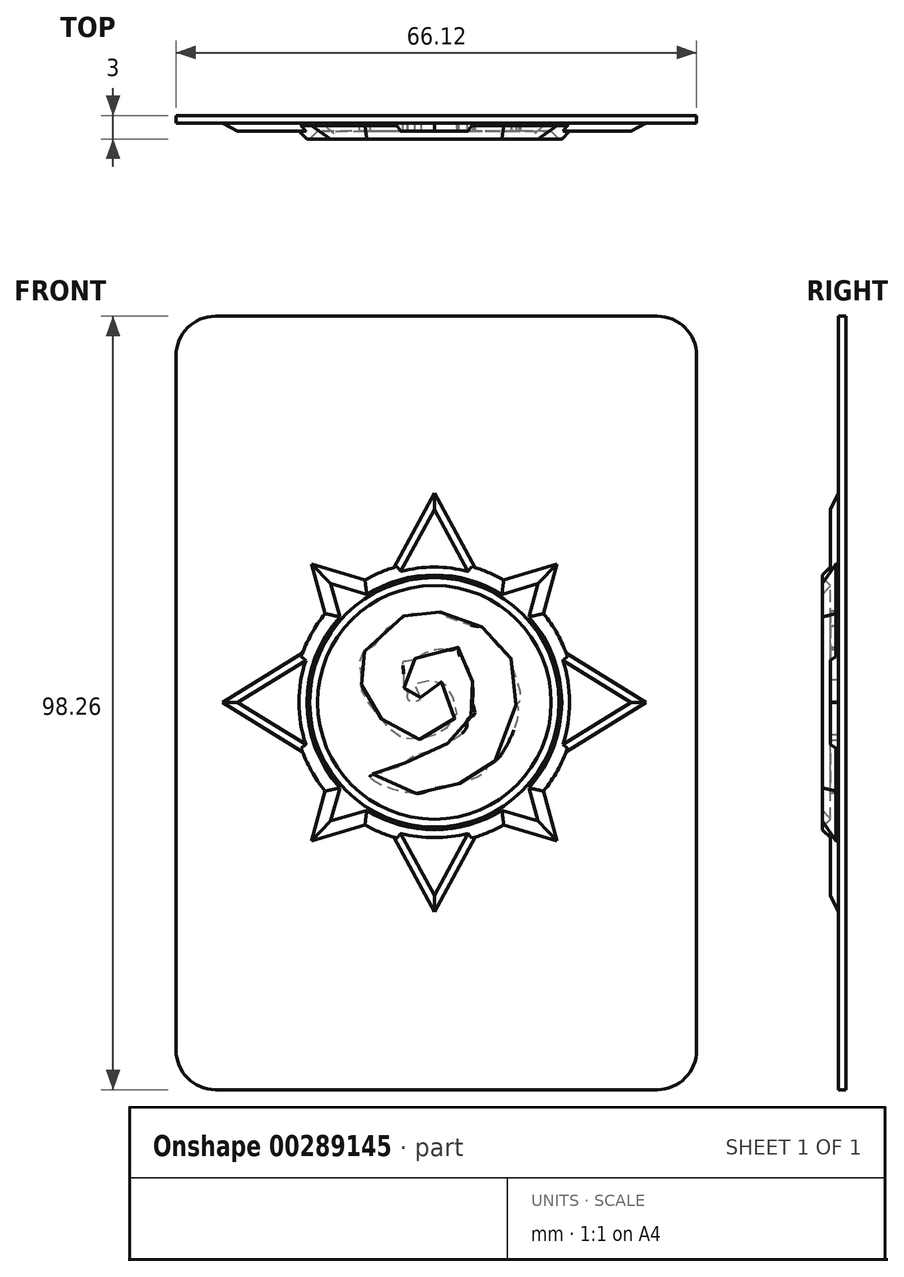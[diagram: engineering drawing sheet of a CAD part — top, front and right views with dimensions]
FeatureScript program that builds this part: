
annotation { "Feature Type Name" : "Feature", "Feature Type Description" : "" }
export const myFeature = defineFeature(function(context is Context, id is Id, definition is map)
    precondition{}
    {
        {
            var Q0;
            Q0=qCreatedBy(makeId("Front.planeOp"),FACE);
            var sketch = newSketch(context, id + "F0", { "sketchPlane" : qUnion([Q0])});
            skArc(sketch, "E0", {"start": v(14.14, 0) * mm, "mid": v(10, 10) * mm, "end": v(0, 14.14) * mm});
            skArc(sketch, "E1", {"start": v(17.88, 0) * mm, "mid": v(12.64, 12.64) * mm, "end": v(0, 17.88) * mm});
            skArc(sketch, "E2", {"start": v(15.77, 0) * mm, "mid": v(11.15, 11.15) * mm, "end": v(0, 15.77) * mm});
            skLineSegment(sketch, "E3", {"start": v(10.28, 11.96) * mm, "end": v(15.6, 17.6) * mm});
            skLineSegment(sketch, "E4", {"start": v(15.6, 17.6) * mm, "end": v(8.8, 15.56) * mm});
            skLineSegment(sketch, "E5", {"start": v(15.6, 17.6) * mm, "end": v(13.88, 11.27) * mm});
            skLineSegment(sketch, "E6", {"start": v(5.15, 17.13) * mm, "end": v(0, 26.62) * mm});
            skLineSegment(sketch, "E7", {"start": v(16.75, 6.27) * mm, "end": v(26.88, 0) * mm});
            skLineSegment(sketch, "E8", {"start": v(0, 26.62) * mm, "end": v(0, 0) * mm});
            skLineSegment(sketch, "E9", {"start": v(26.88, 0) * mm, "end": v(0, 0) * mm});
            skSolve(sketch);
        }
        {
            var Q0;
            {var subQ0=sQuery(id+"F0.wireOp",EDGE,"E0");Q0=makeQuery(id+"F0.imprint","IMPRINT",FACE,{"disambiguationData":[TD([[makeQuery(id+"F0.imprint","IMPRINT",EDGE,{"derivedFrom":subQ0}),1.0]])]});}
            extrude(context, id + "F1", {"entities" : qUnion([Q0]), "depth" : 1 * mm});
        }
        {
            var Q0;
            {var subQ4=sQuery(id+"F0.wireOp",EDGE,"E0");Q0=makeQuery(id+"F0.imprint","IMPRINT",FACE,{"disambiguationData":[TD([[makeQuery(id+"F0.imprint","IMPRINT",EDGE,{"derivedFrom":subQ4}),-1.0]])]});}
            extrude(context, id + "F2", {"entities" : qUnion([Q0]), "operationType" : NewBodyOperationType.ADD, "depth" : 2 * mm});
        }
        {
            var Q0;
            {var subQ0=sQuery(id+"F0.wireOp",EDGE,"E1");var subQ4=sQuery(id+"F0.wireOp",EDGE,"E9");var subQ9=makeQuery(id+"F0.imprint","INTERSECT",VERTEX,{"derivedFrom":[subQ0,subQ4]});Q0=makeQuery(id+"F0.imprint","IMPRINT",FACE,{"disambiguationData":[TD([[makeQuery(id+"F0.imprint","IMPRINT",EDGE,{"disambiguationData":[TD([[subQ9,-1.0]])],"derivedFrom":subQ0}),1.0]])]});}
            var Q1;
            {var subQ5=sQuery(id+"F0.wireOp",EDGE,"E1");var subQ8=makeQuery(id+"F0.imprint","INTERSECT",VERTEX,{"derivedFrom":[subQ5,sQuery(id+"F0.wireOp",EDGE,"E4")]});Q1=makeQuery(id+"F0.imprint","IMPRINT",FACE,{"disambiguationData":[TD([[makeQuery(id+"F0.imprint","IMPRINT",EDGE,{"disambiguationData":[TD([[subQ8,1.0]])],"derivedFrom":subQ5}),1.0]])]});}
            extrude(context, id + "F3", {"entities" : qUnion([Q0, Q1]), "operationType" : NewBodyOperationType.ADD, "depth" : 2 * mm});
        }
        {
            var Q0;
            {var subQ3=sQuery(id+"F0.wireOp",EDGE,"E7");Q0=makeQuery(id+"F0.imprint","IMPRINT",FACE,{"disambiguationData":[TD([[makeQuery(id+"F0.imprint","IMPRINT",EDGE,{"derivedFrom":subQ3}),-1.0]])]});}
            var Q1;
            {var subQ3=sQuery(id+"F0.wireOp",EDGE,"E6");Q1=makeQuery(id+"F0.imprint","IMPRINT",FACE,{"disambiguationData":[TD([[makeQuery(id+"F0.imprint","IMPRINT",EDGE,{"derivedFrom":subQ3}),1.0]])]});}
            extrude(context, id + "F4", {"entities" : qUnion([Q0, Q1]), "operationType" : NewBodyOperationType.ADD, "depth" : 1 * mm});
        }
        {
            var Q0;
            Q0=makeQuery(id+"F2.opExtrude","CAP_EDGE",EDGE,{"disambiguationData":[OSD([sQuery(id+"F0.wireOp",EDGE,"E0")])],"isStart":false});
            chamfer(context, id + "F5", {"entities" : qUnion([Q0]), "width" : 1.7 * mm, "tangentPropagation" : true});
        }
        {
            var Q0;
            {var subQ0=sQuery(id+"F0.wireOp",EDGE,"E5");Q0=makeQuery(id+"F0.imprint","IMPRINT",FACE,{"disambiguationData":[TD([[makeQuery(id+"F0.imprint","IMPRINT",EDGE,{"derivedFrom":subQ0}),-1.0]])]});}
            var Q1;
            {var subQ0=sQuery(id+"F0.wireOp",EDGE,"E4");Q1=makeQuery(id+"F0.imprint","IMPRINT",FACE,{"disambiguationData":[TD([[makeQuery(id+"F0.imprint","IMPRINT",EDGE,{"derivedFrom":subQ0}),1.0]])]});}
            extrude(context, id + "F6", {"entities" : qUnion([Q0, Q1]), "operationType" : NewBodyOperationType.ADD, "depth" : 2 * mm});
        }
        {
            var Q0;
            {var subQ0=sQuery(id+"F0.wireOp",EDGE,"E8");var subQ1=sQuery(id+"F0.wireOp",EDGE,"E1");Q0=makeQuery(id+"F6.boolean.opBoolean","SPLIT",EDGE,{"disambiguationData":[TD([makeQuery(id+"F1.opExtrude","SWEPT_FACE",FACE,{"disambiguationData":[OSD([subQ0])]})])],"derivedFrom":makeQuery(id+"F3.opExtrude","CAP_EDGE",EDGE,{"disambiguationData":[OSD([subQ1])],"isStart":false})});}
            var Q1;
            {var subQ0=sQuery(id+"F0.wireOp",EDGE,"E9");var subQ1=sQuery(id+"F0.wireOp",EDGE,"E1");Q1=makeQuery(id+"F6.boolean.opBoolean","SPLIT",EDGE,{"disambiguationData":[TD([makeQuery(id+"F1.opExtrude","SWEPT_FACE",FACE,{"disambiguationData":[OSD([subQ0])]})])],"derivedFrom":makeQuery(id+"F3.opExtrude","CAP_EDGE",EDGE,{"disambiguationData":[OSD([subQ1])],"isStart":false})});}
            chamfer(context, id + "F7", {"entities" : qUnion([Q0, Q1]), "width" : 1.7 * mm, "tangentPropagation" : true});
        }
        {
            var Q0;
            Q0=makeQuery(id+"F6.opExtrude","CAP_EDGE",EDGE,{"disambiguationData":[OSD([sQuery(id+"F0.wireOp",EDGE,"E4")])],"isStart":false});
            var Q1;
            Q1=makeQuery(id+"F6.opExtrude","CAP_EDGE",EDGE,{"disambiguationData":[OSD([sQuery(id+"F0.wireOp",EDGE,"E5")])],"isStart":false});
            chamfer(context, id + "F8", {"entities" : qUnion([Q0, Q1]), "width" : 1.7 * mm, "tangentPropagation" : true});
        }
        {
            var Q0;
            Q0=makeQuery(id+"F4.opExtrude","CAP_EDGE",EDGE,{"disambiguationData":[OSD([sQuery(id+"F0.wireOp",EDGE,"E6")])],"isStart":false});
            var Q1;
            Q1=makeQuery(id+"F4.opExtrude","CAP_EDGE",EDGE,{"disambiguationData":[OSD([sQuery(id+"F0.wireOp",EDGE,"E7")])],"isStart":false});
            chamfer(context, id + "F9", {"entities" : qUnion([Q0, Q1]), "width" : 1 * mm, "tangentPropagation" : true});
        }
        {
            var Q0;
            Q0=makeQuery(id+"F1.opExtrude","SWEPT_BODY",BODY,{"disambiguationData":[OSD([sQuery(id+"F0.wireOp",EDGE,"E0"),sQuery(id+"F0.wireOp",EDGE,"E8"),sQuery(id+"F0.wireOp",EDGE,"E9")])]});
            var Q1;
            Q1=qCreatedBy(makeId("Right.planeOp"),FACE);
            mirror(context, id + "F10", {"operationType" : NewBodyOperationType.ADD, "entities" : qUnion([Q0]), "mirrorPlane" : qUnion([Q1])});
        }
        {
            var Q0;
            Q0=makeQuery(id+"F1.opExtrude","SWEPT_BODY",BODY,{"disambiguationData":[OSD([sQuery(id+"F0.wireOp",EDGE,"E0"),sQuery(id+"F0.wireOp",EDGE,"E8"),sQuery(id+"F0.wireOp",EDGE,"E9")])]});
            var Q1;
            Q1=qCreatedBy(makeId("Top.planeOp"),FACE);
            mirror(context, id + "F11", {"operationType" : NewBodyOperationType.ADD, "entities" : qUnion([Q0]), "mirrorPlane" : qUnion([Q1])});
        }
        {
            var Q0;
            {var subQ0=sQuery(id+"F0.wireOp",EDGE,"E1");var subQ1=sQuery(id+"F0.wireOp",EDGE,"E8");var subQ2=sQuery(id+"F0.wireOp",EDGE,"E9");var subQ3=sQuery(id+"F0.wireOp",EDGE,"E2");var subQ4=sQuery(id+"F0.wireOp",EDGE,"E0");var subQ5=makeQuery(id+"F6.boolean.opBoolean","MERGE",FACE,{"derivedFrom":[makeQuery(id+"F4.boolean.opBoolean","MERGE",FACE,{"derivedFrom":[makeQuery(id+"F3.boolean.opBoolean","MERGE",FACE,{"derivedFrom":[makeQuery(id+"F2.boolean.opBoolean","MERGE",FACE,{"derivedFrom":[makeQuery(id+"F1.opExtrude","CAP_FACE",FACE,{"disambiguationData":[OSD([subQ4,subQ1,subQ2])],"isStart":true}),makeQuery(id+"F2.opExtrude","CAP_FACE",FACE,{"disambiguationData":[OSD([subQ4,subQ3,subQ1,subQ2])],"isStart":true})]}),makeQuery(id+"F3.opExtrude","CAP_FACE",FACE,{"disambiguationData":[OSD([subQ0,subQ3,subQ1,subQ2])],"isStart":true})]}),makeQuery(id+"F4.opExtrude","CAP_FACE",FACE,{"disambiguationData":[OSD([subQ0,sQuery(id+"F0.wireOp",EDGE,"E7"),subQ2])],"isStart":true}),makeQuery(id+"F4.opExtrude","CAP_FACE",FACE,{"disambiguationData":[OSD([subQ0,sQuery(id+"F0.wireOp",EDGE,"E6"),subQ1])],"isStart":true})]}),makeQuery(id+"F6.opExtrude","CAP_FACE",FACE,{"disambiguationData":[OSD([subQ0,sQuery(id+"F0.wireOp",EDGE,"E4"),sQuery(id+"F0.wireOp",EDGE,"E5")])],"isStart":true})]});var subQ6=makeQuery(id+"F10.boolean.opBoolean","MERGE",FACE,{"derivedFrom":[subQ5,makeQuery(id+"F10.opPattern","COPY",FACE,{"derivedFrom":subQ5,"instanceName":"1"})]});Q0=makeQuery(id+"F11.boolean.opBoolean","MERGE",FACE,{"derivedFrom":[subQ6,makeQuery(id+"F11.opPattern","COPY",FACE,{"derivedFrom":subQ6,"instanceName":"1"})]});}
            extrude(context, id + "F12", {"entities" : qUnion([Q0]), "operationType" : NewBodyOperationType.ADD, "depth" : 1 * mm});
        }
        {
            var Q0;
            {var subQ0=makeQuery(id+"F1.opExtrude","CAP_FACE",FACE,{"disambiguationData":[OSD([sQuery(id+"F0.wireOp",EDGE,"E0"),sQuery(id+"F0.wireOp",EDGE,"E8"),sQuery(id+"F0.wireOp",EDGE,"E9")])],"isStart":false});var subQ1=makeQuery(id+"F10.boolean.opBoolean","MERGE",FACE,{"derivedFrom":[subQ0,makeQuery(id+"F10.opPattern","COPY",FACE,{"derivedFrom":subQ0,"instanceName":"1"})]});Q0=makeQuery(id+"F11.boolean.opBoolean","MERGE",FACE,{"derivedFrom":[subQ1,makeQuery(id+"F11.opPattern","COPY",FACE,{"derivedFrom":subQ1,"instanceName":"1"})]});}
            var sketch = newSketch(context, id + "F13", { "sketchPlane" : qUnion([Q0])});
            skFitSpline(sketch, "E10", {"points": [v(-1.73, 0.6) * mm, v(-2.52, 2.4) * mm, v(-0.1, 2.8) * mm, v(1.6, 2.09) * mm, v(2.61, -0.27) * mm, v(2.54, -2.15) * mm, v(0.25, -4.14) * mm, v(-0.1, -4.14) * mm, v(-2.54, -4.82) * mm, v(-4.79, -4.1) * mm, v(-6.6, -2.29) * mm, v(-8.13, -0.27) * mm, v(-9.03, 1.03) * mm, v(-9.26, 2.96) * mm, v(-9.38, 4.76) * mm, v(-9.5, 6.06) * mm, v(-8.06, 6.8) * mm, v(-6.39, 8.94) * mm, v(-2.3, 11.56) * mm, v(-0.5, 11.26) * mm, v(0.57, 11.59) * mm, v(1.08, 11.17) * mm, v(5.44, 9.66) * mm, v(5.9, 9.68) * mm, v(6.37, 9.22) * mm, v(9.32, 5.95) * mm, v(9.76, 5.74) * mm, v(9.74, 5.2) * mm, v(10.92, 0.26) * mm, v(10.37, -0.27) * mm, v(10.64, -0.82) * mm, v(8.17, -7.04) * mm, v(6.88, -7.94) * mm, v(6.27, -8.93) * mm, v(2.27, -10.5) * mm, v(-0.1, -10.9) * mm, v(-1.86, -11.53) * mm, v(-6.88, -10.4) * mm, v(-8.11, -9.27) * mm, v(-6.42, -8.83) * mm, v(-5.65, -8.46) * mm, v(-4.18, -8.04) * mm, v(-2.93, -6.96) * mm, v(-0.1, -6.03) * mm, v(2.68, -4.53) * mm, v(4.1, -3.13) * mm, v(4.2, -2.17) * mm, v(5.09, -1.53) * mm, v(4.89, -0.27) * mm, v(4.94, 1.79) * mm, v(4.23, 4.5) * mm, v(3.12, 6.16) * mm, v(3.05, 6.97) * mm, v(2.38, 6.73) * mm, v(-0.1, 6.63) * mm, v(-3.1, 5.3) * mm, v(-3.98, 5.13) * mm, v(-3.96, 4.34) * mm, v(-3.71, 1.5) * mm, v(-3.44, 1.4) * mm, v(-3.44, 1.07) * mm, v(-3.2, 0.24) * mm, v(-1.73, 0.6) * mm]});
            skSolve(sketch);
        }
        {
            var Q0;
            Q0=makeQuery(id+"F13.imprint","IMPRINT",FACE,{"disambiguationData":[TD([[makeQuery(id+"F13.imprint","IMPRINT",EDGE,{"derivedFrom":sQuery(id+"F13.wireOp",EDGE,"E10")}),-1.0]])]});
            extrude(context, id + "F14", {"entities" : qUnion([Q0]), "operationType" : NewBodyOperationType.REMOVE, "oppositeDirection" : true, "depth" : 1 * mm});
        }
        {
            var Q0;
            Q0=makeQuery(id+"F12.opExtrude","CAP_FACE",FACE,{"disambiguationData":[OSD([sQuery(id+"F0.wireOp",EDGE,"E0"),sQuery(id+"F0.wireOp",EDGE,"E1"),sQuery(id+"F0.wireOp",EDGE,"E2"),sQuery(id+"F0.wireOp",EDGE,"E4"),sQuery(id+"F0.wireOp",EDGE,"E5"),sQuery(id+"F0.wireOp",EDGE,"E6"),sQuery(id+"F0.wireOp",EDGE,"E7"),sQuery(id+"F0.wireOp",EDGE,"E8"),sQuery(id+"F0.wireOp",EDGE,"E9")])],"isStart":false});
            var sketch = newSketch(context, id + "F15", { "sketchPlane" : qUnion([Q0])});
            skLineSegment(sketch, "E11.bottom", {"start": v(-33.3, 49.06) * mm, "end": v(32.8, 49.06) * mm});
            skLineSegment(sketch, "E11.top", {"start": v(-33.3, -49.2) * mm, "end": v(32.8, -49.2) * mm});
            skLineSegment(sketch, "E11.left", {"start": v(-33.3, 49.06) * mm, "end": v(-33.3, -49.2) * mm});
            skLineSegment(sketch, "E11.right", {"start": v(32.8, 49.06) * mm, "end": v(32.8, -49.2) * mm});
            skSolve(sketch);
        }
        {
            var Q0;
            Q0=makeQuery(id+"F15.imprint","IMPRINT",FACE,{"disambiguationData":[TD([[makeQuery(id+"F15.imprint","IMPRINT",EDGE,{"derivedFrom":sQuery(id+"F15.wireOp",EDGE,"E11.bottom")}),-1.0]])]});
            extrude(context, id + "F16", {"entities" : qUnion([Q0]), "operationType" : NewBodyOperationType.ADD, "oppositeDirection" : true, "depth" : 1 * mm});
        }
        {
            var Q0;
            Q0=makeQuery(id+"F16.opExtrude","SWEPT_EDGE",EDGE,{"disambiguationData":[OSD([sQuery(id+"F15.wireOp",EDGE,"E11.bottom"),sQuery(id+"F15.wireOp",EDGE,"E11.right")])]});
            var Q1;
            Q1=makeQuery(id+"F16.opExtrude","SWEPT_EDGE",EDGE,{"disambiguationData":[OSD([sQuery(id+"F15.wireOp",EDGE,"E11.bottom"),sQuery(id+"F15.wireOp",EDGE,"E11.left")])]});
            var Q2;
            Q2=makeQuery(id+"F16.opExtrude","SWEPT_EDGE",EDGE,{"disambiguationData":[OSD([sQuery(id+"F15.wireOp",EDGE,"E11.top"),sQuery(id+"F15.wireOp",EDGE,"E11.left")])]});
            var Q3;
            Q3=makeQuery(id+"F16.opExtrude","SWEPT_EDGE",EDGE,{"disambiguationData":[OSD([sQuery(id+"F15.wireOp",EDGE,"E11.top"),sQuery(id+"F15.wireOp",EDGE,"E11.right")])]});
            fillet(context, id + "F17", {"entities" : qUnion([Q0, Q1, Q2, Q3]), "radius" : 5 * mm, "tangentPropagation" : true, "allowEdgeOverflow" : false});
        }
    });
